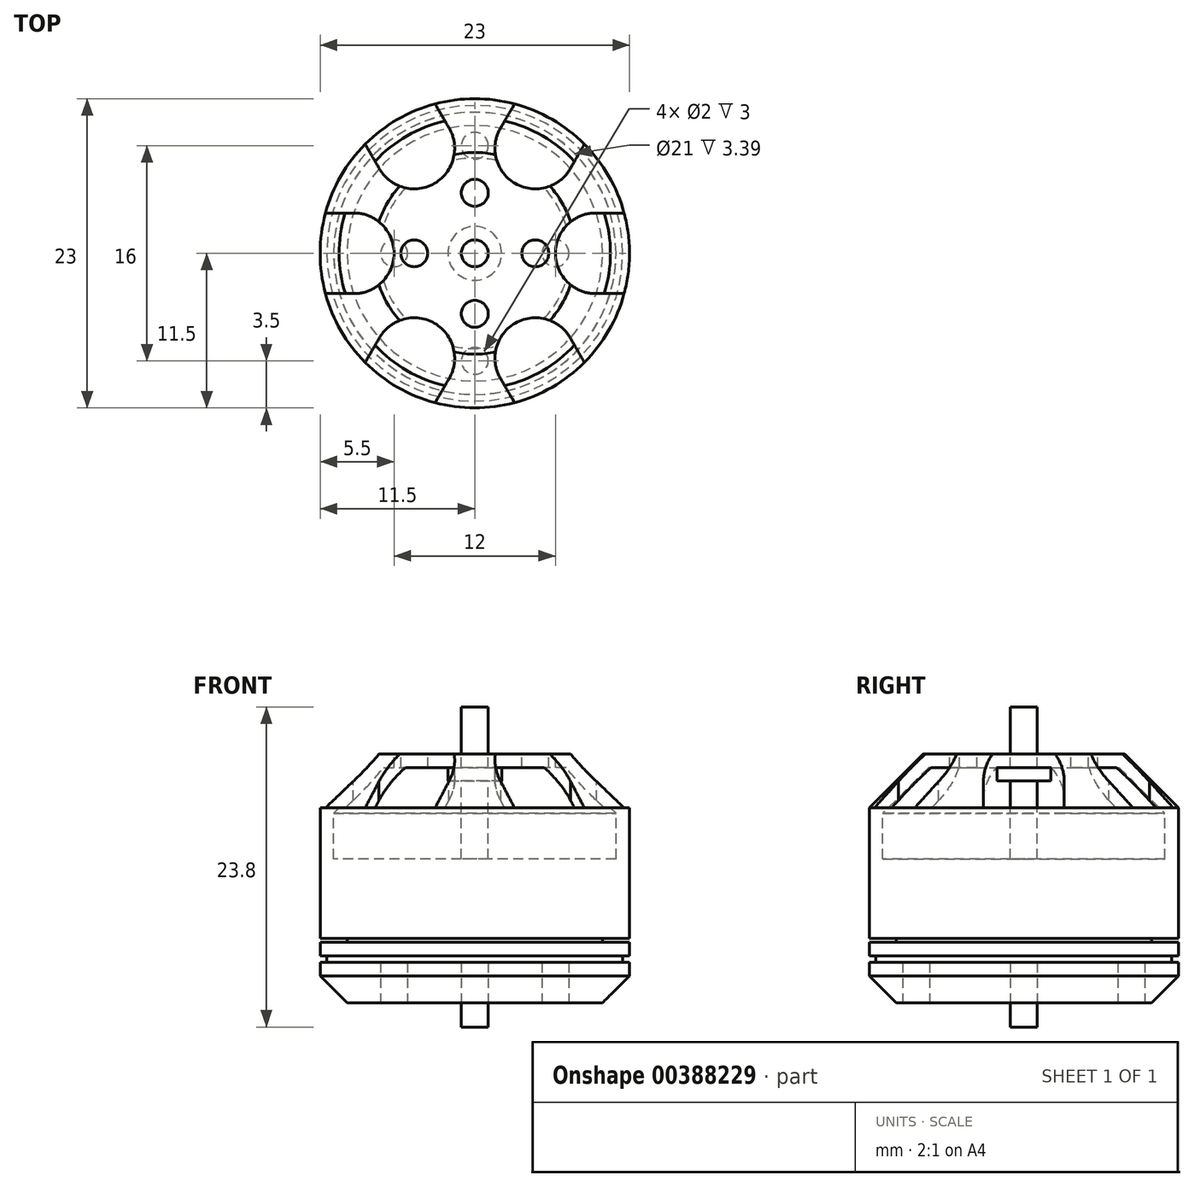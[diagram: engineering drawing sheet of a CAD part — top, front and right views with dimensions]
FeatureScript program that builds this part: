
annotation { "Feature Type Name" : "Feature", "Feature Type Description" : "" }
export const myFeature = defineFeature(function(context is Context, id is Id, definition is map)
    precondition{}
    {
        {
            var Q0;
            Q0=qCreatedBy(makeId("Front.planeOp"),FACE);
            var sketch = newSketch(context, id + "F0", { "sketchPlane" : qUnion([Q0])});
            skLineSegment(sketch, "E0", {"start": v(0, 22) * mm, "end": v(0, 0) * mm});
            skLineSegment(sketch, "E1", {"start": v(1, 0) * mm, "end": v(9.5, 0) * mm});
            skLineSegment(sketch, "E2", {"start": v(9.5, 0) * mm, "end": v(11.5, 2) * mm});
            skLineSegment(sketch, "E3", {"start": v(11.5, 2) * mm, "end": v(11.5, 3) * mm});
            skLineSegment(sketch, "E4", {"start": v(11.5, 14.5) * mm, "end": v(7.5, 18.5) * mm});
            skLineSegment(sketch, "E5", {"start": v(7.5, 18.5) * mm, "end": v(1, 18.5) * mm});
            skLineSegment(sketch, "E6", {"start": v(1, 18.5) * mm, "end": v(1, 22) * mm});
            skLineSegment(sketch, "E7", {"start": v(1, 22) * mm, "end": v(0, 22) * mm});
            skLineSegment(sketch, "E8", {"start": v(0, 0) * mm, "end": v(0, -1.8) * mm});
            skLineSegment(sketch, "E9", {"start": v(0, -1.8) * mm, "end": v(1, -1.8) * mm});
            skLineSegment(sketch, "E10", {"start": v(1, -1.8) * mm, "end": v(1, 0) * mm});
            skLineSegment(sketch, "E11", {"start": v(2, 17.5) * mm, "end": v(7.09, 17.5) * mm});
            skLineSegment(sketch, "E12", {"start": v(7.09, 17.5) * mm, "end": v(10.5, 14.09) * mm});
            skLineSegment(sketch, "E13", {"start": v(10.5, 14.09) * mm, "end": v(10.5, 10.7) * mm});
            skLineSegment(sketch, "E14", {"start": v(10.5, 10.7) * mm, "end": v(1, 10.7) * mm});
            skLineSegment(sketch, "E15", {"start": v(1, 10.7) * mm, "end": v(1, 16.5) * mm});
            skLineSegment(sketch, "E16", {"start": v(1, 16.5) * mm, "end": v(2, 16.5) * mm});
            skLineSegment(sketch, "E17", {"start": v(2, 16.5) * mm, "end": v(2, 17.5) * mm});
            skLineSegment(sketch, "E18", {"start": v(11.5, 3) * mm, "end": v(11, 3) * mm});
            skLineSegment(sketch, "E19", {"start": v(11, 3) * mm, "end": v(11, 3.5) * mm});
            skLineSegment(sketch, "E20", {"start": v(11, 3.5) * mm, "end": v(11.5, 3.5) * mm});
            skLineSegment(sketch, "E21", {"start": v(11.5, 4.5) * mm, "end": v(9.5, 4.5) * mm});
            skLineSegment(sketch, "E22", {"start": v(9.5, 4.5) * mm, "end": v(9.5, 4.8) * mm});
            skLineSegment(sketch, "E23", {"start": v(9.5, 4.8) * mm, "end": v(11.5, 4.8) * mm});
            skLineSegment(sketch, "E24.trimOffspring", {"start": v(11.5, 3.5) * mm, "end": v(11.5, 4.5) * mm});
            skLineSegment(sketch, "E25.trimOffspring", {"start": v(11.5, 4.8) * mm, "end": v(11.5, 14.5) * mm});
            skSolve(sketch);
        }
        {
            var Q0;
            Q0=makeQuery(id+"F0.imprint","IMPRINT",FACE,{"disambiguationData":[TD([[makeQuery(id+"F0.imprint","IMPRINT",EDGE,{"derivedFrom":sQuery(id+"F0.wireOp",EDGE,"E0")}),1.0]])]});
            var Q1;
            Q1=sQuery(id+"F0.wireOp",EDGE,"E0");
            revolve(context, id + "F1", {"entities" : qUnion([Q0]), "axis" : qUnion([Q1]), "revolveType" : RevolveType.FULL});
        }
        {
            var Q0;
            Q0=makeQuery(id+"F1.opRevolve","SWEPT_FACE",FACE,{"disambiguationData":[OSD([sQuery(id+"F0.wireOp",EDGE,"E5")])]});
            var sketch = newSketch(context, id + "F2", { "sketchPlane" : qUnion([Q0])});
            skCircle(sketch, "E26", {"center": v(0, 0) * mm, "radius": 4.5 * mm, "construction": true});
            skLineSegment(sketch, "E27", {"start": v(0, 0) * mm, "end": v(-9, 0) * mm, "construction": true});
            skCircle(sketch, "E28", {"center": v(4.5, 0) * mm, "radius": 1 * mm});
            skCircle(sketch, "E29.1.0", {"center": v(0, 4.5) * mm, "radius": 1 * mm});
            skCircle(sketch, "E29.2.0", {"center": v(-4.5, 0) * mm, "radius": 1 * mm});
            skCircle(sketch, "E29.3.0", {"center": v(0, -4.5) * mm, "radius": 1 * mm});
            skArc(sketch, "E30", {"start": v(-9.05, -3) * mm, "mid": v(-6, 0) * mm, "end": v(-9.05, 3) * mm});
            skLineSegment(sketch, "E31", {"start": v(-8.95, -3) * mm, "end": v(-15.53, -3) * mm});
            skLineSegment(sketch, "E32", {"start": v(-15.53, -3) * mm, "end": v(-15.53, 3) * mm});
            skLineSegment(sketch, "E33", {"start": v(-15.53, 3) * mm, "end": v(-8.95, 3) * mm});
            skLineSegment(sketch, "E34.1.0", {"start": v(-5.17, -14.95) * mm, "end": v(-10.36, -11.95) * mm});
            skLineSegment(sketch, "E34.1.1", {"start": v(-1.88, -9.25) * mm, "end": v(-5.17, -14.95) * mm});
            skArc(sketch, "E34.1.2", {"start": v(-1.93, -9.34) * mm, "mid": v(-3, -5.2) * mm, "end": v(-7.12, -6.34) * mm});
            skLineSegment(sketch, "E34.1.3", {"start": v(-10.36, -11.95) * mm, "end": v(-7.07, -6.25) * mm});
            skLineSegment(sketch, "E34.2.0", {"start": v(10.36, -11.95) * mm, "end": v(5.17, -14.95) * mm});
            skLineSegment(sketch, "E34.2.1", {"start": v(7.07, -6.25) * mm, "end": v(10.36, -11.95) * mm});
            skArc(sketch, "E34.2.2", {"start": v(7.12, -6.34) * mm, "mid": v(3, -5.2) * mm, "end": v(1.93, -9.34) * mm});
            skLineSegment(sketch, "E34.2.3", {"start": v(5.17, -14.95) * mm, "end": v(1.88, -9.25) * mm});
            skLineSegment(sketch, "E34.3.0", {"start": v(15.53, 3) * mm, "end": v(15.53, -3) * mm});
            skLineSegment(sketch, "E34.3.1", {"start": v(8.95, 3) * mm, "end": v(15.53, 3) * mm});
            skArc(sketch, "E34.3.2", {"start": v(9.05, 3) * mm, "mid": v(6, 0) * mm, "end": v(9.05, -3) * mm});
            skLineSegment(sketch, "E34.3.3", {"start": v(15.53, -3) * mm, "end": v(8.95, -3) * mm});
            skLineSegment(sketch, "E34.4.0", {"start": v(5.17, 14.95) * mm, "end": v(10.36, 11.95) * mm});
            skLineSegment(sketch, "E34.4.1", {"start": v(1.88, 9.25) * mm, "end": v(5.17, 14.95) * mm});
            skArc(sketch, "E34.4.2", {"start": v(1.93, 9.34) * mm, "mid": v(3, 5.2) * mm, "end": v(7.12, 6.34) * mm});
            skLineSegment(sketch, "E34.4.3", {"start": v(10.36, 11.95) * mm, "end": v(7.07, 6.25) * mm});
            skLineSegment(sketch, "E34.5.0", {"start": v(-10.36, 11.95) * mm, "end": v(-5.17, 14.95) * mm});
            skLineSegment(sketch, "E34.5.1", {"start": v(-7.07, 6.25) * mm, "end": v(-10.36, 11.95) * mm});
            skArc(sketch, "E34.5.2", {"start": v(-7.12, 6.34) * mm, "mid": v(-3, 5.2) * mm, "end": v(-1.93, 9.34) * mm});
            skLineSegment(sketch, "E34.5.3", {"start": v(-5.17, 14.95) * mm, "end": v(-1.88, 9.25) * mm});
            skSolve(sketch);
        }
        {
            var Q0;
            Q0 = qSketchRegion(id + "F2", true);
            extrude(context, id + "F3", {"entities" : qUnion([Q0]), "operationType" : NewBodyOperationType.REMOVE, "oppositeDirection" : true, "depth" : 4 * mm});
        }
        {
            var Q0;
            Q0=makeQuery(id+"F1.opRevolve","SWEPT_FACE",FACE,{"disambiguationData":[OSD([sQuery(id+"F0.wireOp",EDGE,"E1")])]});
            var sketch = newSketch(context, id + "F4", { "sketchPlane" : qUnion([Q0])});
            skCircle(sketch, "E35", {"center": v(0, 0) * mm, "radius": 6 * mm, "construction": true});
            skCircle(sketch, "E36", {"center": v(0, 0) * mm, "radius": 8 * mm, "construction": true});
            skCircle(sketch, "E37", {"center": v(6, 0) * mm, "radius": 1 * mm});
            skCircle(sketch, "E38", {"center": v(-6, 0) * mm, "radius": 1 * mm});
            skCircle(sketch, "E39", {"center": v(0, -8) * mm, "radius": 1 * mm});
            skCircle(sketch, "E40", {"center": v(0, 8) * mm, "radius": 1 * mm});
            skSolve(sketch);
        }
        {
            var Q0;
            Q0 = qSketchRegion(id + "F4", true);
            extrude(context, id + "F5", {"entities" : qUnion([Q0]), "operationType" : NewBodyOperationType.REMOVE, "oppositeDirection" : true, "depth" : 3 * mm});
        }
    });
